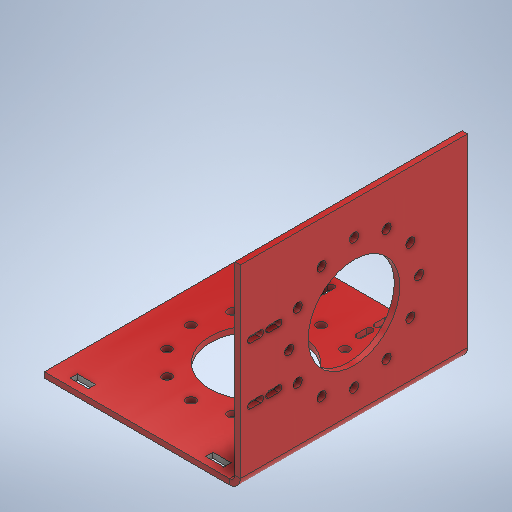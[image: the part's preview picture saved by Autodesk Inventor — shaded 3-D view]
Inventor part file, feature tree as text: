
AUTODESK INVENTOR PART (.ipt)
format: ipt  version: 2025 (Build 290162000, 162)  size: 493,056 bytes
history: native  units: in
note: dims shown in document units (in); Inventor stores cm internally (conversion verified against a paired STEP export)
features: sketch x9, sheet_metal_op x6, other x4
ambient origin geometry x8: Origin, YZ Plane, XZ Plane, XY Plane, X Axis, Y Axis, Z Axis, Center Point
bodies: Solid1 (feature_tree)
feature tree (19):
  sheet_metal_op  "Face1"
  sheet_metal_op  "Flange1"
  sheet_metal_op  "Unfold1"
  sheet_metal_op  "Refold1"
  sketch  "Sketch1"  dims[d0=4.2126in]
  sketch  "Sketch Circular Pattern1"  dims[d1=4.8819in]
  sketch  "Sketch Rectangular Pattern1"  dims[d2=1.9685in]
  other  "Plate1"
  sketch  "Sketch2"  dims[d3=2.4409in]
  other  "Plate2"
  sheet_metal_op  "Bend1"
  sheet_metal_op  "Corner1"
  sketch  "Sketch3"  dims[d6=1.3976in]
  sketch  "Sketch Circular Pattern2"  dims[d4=2.1063in]
  sketch  "Sketch Rectangular Pattern2"  dims[d5=0.1969in]
  sketch  "Sketch4"  dims[d11=0.1378in d12=0.3543in d13=0.0689in d14=0.6102in d15=2.2244in d16=0.7874in d18=1.2205in d19=0.7874in d21=0.3937in d24=0.1181in d25=0.1181in d26=0.0591in d27=0.2362in d28=0.1181in d29=4.2126in d30=90.0deg d31=0.1181in d32=0.4724in d33=0.1181in d34=0.1181in d35=1.9685in d36=2.1063in d37=2.4409in d38=0.1969in d39=1.3976in d40=4.7244in d42=360.0deg d44=0.1378in d45=0.3543in d46=0.0689in d47=0.6102in d48=2.2244in d49=0.7874in d51=1.2205in d52=0.7874in d54=0.3937in d57=0.1181in d58=0.0in d59=0.3937in d60=0.1575in d61=0.1575in d62=0.5118in d63=0.7874in d65=2.9134in d66=0.7874in d68=4.4094in d71=0.1181in d72=0.0in]
  sketch  "Sketch Rectangular Pattern3"  dims[d7=4.7244in d9=360.0deg]
  other  "Cut1"
  other  "Cut2"
